# Revit family: PlumbingFixture_Sink_Oliveri_ST-BL1590U
name_source: partatom
category: Plumbing Fixtures
revit_build: Autodesk Revit Architecture 2013 (Build: 20120221_2030(x64)
units: mm (PartAtom-declared; Revit-internal decimal feet)

## types (4) — shared parameters
Assembly Code = D2010410
CW Connection = No
Description = Mega Bowl undermount sink
HW Connection = No
Manufacturer = OLIVERI
ModifiedIssue_ANZRS = 20160114 $
Oliveri_DimDepth = 450 mm  [stored 1.47638 ft]
Oliveri_DimHeight = 200 mm  [stored 0.656168 ft]
Oliveri_DimMountingHeight = 900 mm  [stored 2.95276 ft]
Oliveri_DimWidth = 760 mm
Oliveri_WasteType = Waste_Oliveri_90mm-Basket : AC14 - 90mm Basket Waste
PlumbingMaterial_Oliveri = Metal_Stainless-Steel-Black_Oliveri
URL = http://www.oliveri.com.au
Vent Connection = No
Waste Connection = No

## per-type parameters (varying)
| type | Model | PlumbingMaterial_ANZRS | Tapware | Type Comments | VT0392_Mask | VT0403_Mask |
| w/- Tap VT0392B | ST-BL1590U-VT0392B | Granite_Polished_Black_Oliveri | PlubingFixture_Taps_Oliveri_VT0392 : B | ST-BL1590U-VT0392B | Yes | No |
| w/- Tap VT0403C | ST-BL1590U-VT0403C | Metal_Stainless-Steel-Polished_Oliveri | PlubingFixture_Taps_Oliveri_VT0403 : C | ST-BL1590U-VT0403C | No | Yes |
| w/- Tap VT0403B | ST-BL1590U-VT0403B | Metal_Stainless-Steel-Polished_Oliveri | PlubingFixture_Taps_Oliveri_VT0403 : B | ST-BL1590U-VT0403B | No | Yes |
| w/- Tap VT0392C | ST-BL1590U-VT0392C | Metal_Stainless-Steel-Polished_Oliveri | PlubingFixture_Taps_Oliveri_VT0392 : C | ST-BL1590U-VT0392C | Yes | No |

note: [stored X ft] marks values corroborated as IEEE doubles in the binary element streams (Revit-internal decimal feet)

## geometry (parser evidence)
native form markers: Blend x18, Sweep x7
no freeform markers — native parametric forms only
